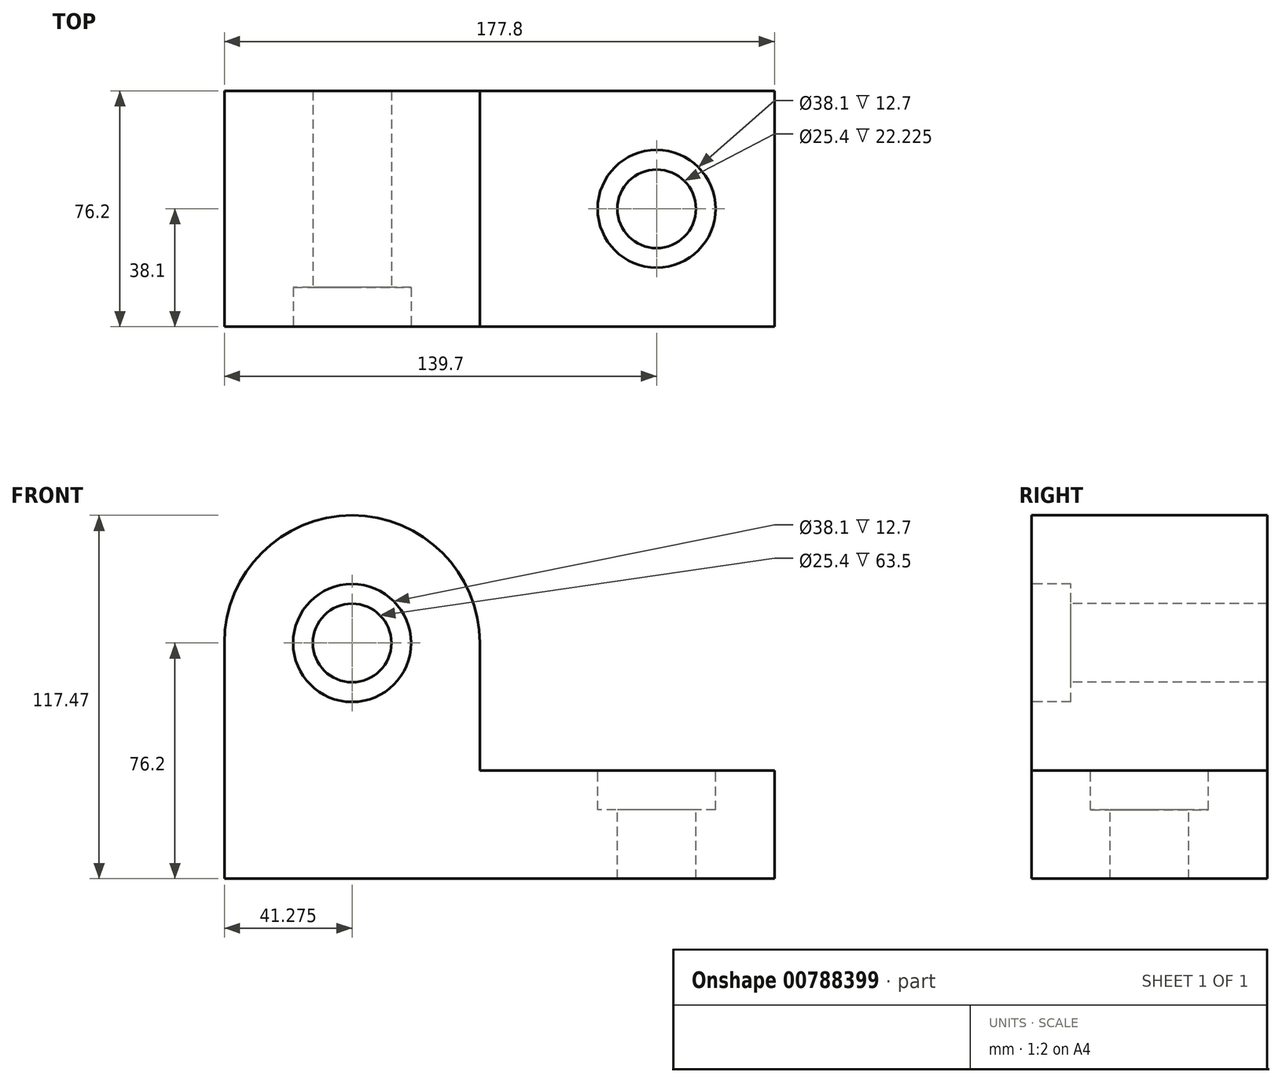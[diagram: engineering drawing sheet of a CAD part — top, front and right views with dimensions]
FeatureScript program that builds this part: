
annotation { "Feature Type Name" : "Feature", "Feature Type Description" : "" }
export const myFeature = defineFeature(function(context is Context, id is Id, definition is map)
    precondition{}
    {
        {
            var Q0;
            Q0=qCreatedBy(makeId("Front.planeOp"),FACE);
            var sketch = newSketch(context, id + "F0", { "sketchPlane" : qUnion([Q0])});
            skLineSegment(sketch, "E0", {"start": v(0, 0) * mm, "end": v(177.8, 0) * mm});
            skLineSegment(sketch, "E1", {"start": v(177.8, 0) * mm, "end": v(177.8, 34.93) * mm});
            skLineSegment(sketch, "E2", {"start": v(177.8, 34.93) * mm, "end": v(82.55, 34.93) * mm});
            skLineSegment(sketch, "E3", {"start": v(82.55, 34.93) * mm, "end": v(82.55, 161.92) * mm});
            skLineSegment(sketch, "E4", {"start": v(82.55, 161.92) * mm, "end": v(0, 161.92) * mm});
            skLineSegment(sketch, "E5", {"start": v(0, 161.92) * mm, "end": v(0, 0) * mm});
            skSolve(sketch);
        }
        {
            var Q0;
            Q0 = qSketchRegion(id + "F0", true);
            extrude(context, id + "F1", {"entities" : qUnion([Q0]), "depth" : 76.2 * mm, "offsetDistance" : 25.4 * mm});
        }
        {
            var Q0;
            Q0=makeQuery(id+"F1.opExtrude","CAP_FACE",FACE,{"disambiguationData":[OSD([sQuery(id+"F0.wireOp",EDGE,"E0"),sQuery(id+"F0.wireOp",EDGE,"E1"),sQuery(id+"F0.wireOp",EDGE,"E2"),sQuery(id+"F0.wireOp",EDGE,"E3"),sQuery(id+"F0.wireOp",EDGE,"E4"),sQuery(id+"F0.wireOp",EDGE,"E5")])],"isStart":false});
            var sketch = newSketch(context, id + "F2", { "sketchPlane" : qUnion([Q0])});
            skLineSegment(sketch, "E6", {"start": v(0, 0) * mm, "end": v(0, 76.2) * mm, "construction": true});
            skLineSegment(sketch, "E7", {"start": v(0, 76.2) * mm, "end": v(82.55, 76.2) * mm, "construction": true});
            skArc(sketch, "E8", {"start": v(82.55, 76.2) * mm, "mid": v(41.27, 117.47) * mm, "end": v(0, 76.2) * mm});
            skSolve(sketch);
        }
        {
            var Q0;
            Q0 = qSketchRegion(id + "F2", true);
            var Q1;
            {var subQ0=sQuery(id+"F2.wireOp",EDGE,"E8");Q1=makeQuery(id+"F2.imprint","IMPRINT",FACE,{"disambiguationData":[TD([[makeQuery(id+"F2.imprint","IMPRINT",EDGE,{"derivedFrom":subQ0}),-1.0]])]});}
            extrude(context, id + "F3", {"entities" : qUnion([Q0, Q1]), "operationType" : NewBodyOperationType.REMOVE, "endBound" : BoundingType.UP_TO_NEXT, "oppositeDirection" : true, "depth" : 25.4 * mm, "offsetDistance" : 25.4 * mm});
        }
        {
            var Q0;
            Q0=makeQuery(id+"F1.opExtrude","SWEPT_FACE",FACE,{"disambiguationData":[OSD([sQuery(id+"F0.wireOp",EDGE,"E2")])]});
            var sketch = newSketch(context, id + "F4", { "sketchPlane" : qUnion([Q0])});
            skLineSegment(sketch, "E9", {"start": v(177.8, -38.1) * mm, "end": v(139.7, -38.1) * mm, "construction": true});
            skCircle(sketch, "E10", {"center": v(139.7, -38.1) * mm, "radius": 6.35 * mm});
            skCircle(sketch, "E11", {"center": v(139.7, -38.1) * mm, "radius": 19.05 * mm});
            skSolve(sketch);
        }
        {
            var Q0;
            Q0 = qSketchRegion(id + "F4", true);
            extrude(context, id + "F5", {"entities" : qUnion([Q0]), "operationType" : NewBodyOperationType.REMOVE, "oppositeDirection" : true, "depth" : 12.7 * mm, "offsetDistance" : 25.4 * mm});
        }
        {
            var Q0;
            Q0=makeQuery(id+"F5.boolean.opBoolean","SPLIT",FACE,{"disambiguationData":[TD([makeQuery(id+"F5.opExtrude","SWEPT_FACE",FACE,{"disambiguationData":[OSD([sQuery(id+"F4.wireOp",EDGE,"E10")])]})])],"derivedFrom":makeQuery(id+"F1.opExtrude","SWEPT_FACE",FACE,{"disambiguationData":[OSD([sQuery(id+"F0.wireOp",EDGE,"E2")])]})});
            extrude(context, id + "F6", {"entities" : qUnion([Q0]), "operationType" : NewBodyOperationType.REMOVE, "oppositeDirection" : true, "depth" : 76.2 * mm, "offsetDistance" : 25.4 * mm});
        }
        {
            var Q0;
            Q0=makeQuery(id+"F1.opExtrude","CAP_FACE",FACE,{"disambiguationData":[OSD([sQuery(id+"F0.wireOp",EDGE,"E0"),sQuery(id+"F0.wireOp",EDGE,"E1"),sQuery(id+"F0.wireOp",EDGE,"E2"),sQuery(id+"F0.wireOp",EDGE,"E3"),sQuery(id+"F0.wireOp",EDGE,"E4"),sQuery(id+"F0.wireOp",EDGE,"E5")])],"isStart":false});
            var sketch = newSketch(context, id + "F7", { "sketchPlane" : qUnion([Q0])});
            skLineSegment(sketch, "E12", {"start": v(0, 0) * mm, "end": v(0, 76.2) * mm, "construction": true});
            skLineSegment(sketch, "E13", {"start": v(0, 76.2) * mm, "end": v(41.27, 76.2) * mm, "construction": true});
            skCircle(sketch, "E14", {"center": v(41.27, 76.2) * mm, "radius": 19.05 * mm});
            skCircle(sketch, "E15", {"center": v(41.27, 76.2) * mm, "radius": 6.35 * mm});
            skSolve(sketch);
        }
        {
            var Q0;
            Q0=makeQuery(id+"F7.imprint","IMPRINT",FACE,{"disambiguationData":[TD([[makeQuery(id+"F7.imprint","IMPRINT",EDGE,{"derivedFrom":sQuery(id+"F7.wireOp",EDGE,"E14")}),1.0]])]});
            extrude(context, id + "F8", {"entities" : qUnion([Q0]), "operationType" : NewBodyOperationType.REMOVE, "oppositeDirection" : true, "depth" : 12.7 * mm, "offsetDistance" : 25.4 * mm});
        }
        {
            var Q0;
            Q0=makeQuery(id+"F8.boolean.opBoolean","SPLIT",FACE,{"disambiguationData":[TD([makeQuery(id+"F8.opExtrude","SWEPT_FACE",FACE,{"disambiguationData":[OSD([sQuery(id+"F7.wireOp",EDGE,"E15")])]})])],"derivedFrom":makeQuery(id+"F1.opExtrude","CAP_FACE",FACE,{"disambiguationData":[OSD([sQuery(id+"F0.wireOp",EDGE,"E0"),sQuery(id+"F0.wireOp",EDGE,"E1"),sQuery(id+"F0.wireOp",EDGE,"E2"),sQuery(id+"F0.wireOp",EDGE,"E3"),sQuery(id+"F0.wireOp",EDGE,"E4"),sQuery(id+"F0.wireOp",EDGE,"E5")])],"isStart":false})});
            extrude(context, id + "F9", {"entities" : qUnion([Q0]), "operationType" : NewBodyOperationType.REMOVE, "oppositeDirection" : true, "depth" : 127 * mm, "offsetDistance" : 25.4 * mm});
        }
        {
            var Q0;
            Q0=makeQuery(id+"F8.boolean.opBoolean","COPY",FACE,{"derivedFrom":makeQuery(id+"F8.opExtrude","CAP_FACE",FACE,{"disambiguationData":[OSD([sQuery(id+"F7.wireOp",EDGE,"E14"),sQuery(id+"F7.wireOp",EDGE,"E15")])],"isStart":false})});
            var sketch = newSketch(context, id + "F10", { "sketchPlane" : qUnion([Q0])});
            skCircle(sketch, "E16", {"center": v(41.27, 76.2) * mm, "radius": 12.7 * mm});
            skSolve(sketch);
        }
        {
            var Q0;
            Q0=makeQuery(id+"F10.imprint","IMPRINT",FACE,{"disambiguationData":[TD([[makeQuery(id+"F10.imprint","IMPRINT",EDGE,{"derivedFrom":sQuery(id+"F10.wireOp",EDGE,"E16")}),1.0]])]});
            extrude(context, id + "F11", {"entities" : qUnion([Q0]), "operationType" : NewBodyOperationType.REMOVE, "oppositeDirection" : true, "depth" : 152.4 * mm, "offsetDistance" : 25.4 * mm});
        }
        {
            var Q0;
            Q0=makeQuery(id+"F5.boolean.opBoolean","COPY",FACE,{"derivedFrom":makeQuery(id+"F5.opExtrude","CAP_FACE",FACE,{"disambiguationData":[OSD([sQuery(id+"F4.wireOp",EDGE,"E10"),sQuery(id+"F4.wireOp",EDGE,"E11")])],"isStart":false})});
            var sketch = newSketch(context, id + "F12", { "sketchPlane" : qUnion([Q0])});
            skCircle(sketch, "E17", {"center": v(139.7, -38.1) * mm, "radius": 12.7 * mm});
            skSolve(sketch);
        }
        {
            var Q0;
            Q0 = qSketchRegion(id + "F12", true);
            extrude(context, id + "F13", {"entities" : qUnion([Q0]), "operationType" : NewBodyOperationType.REMOVE, "oppositeDirection" : true, "depth" : 127 * mm, "offsetDistance" : 25.4 * mm});
        }
    });
